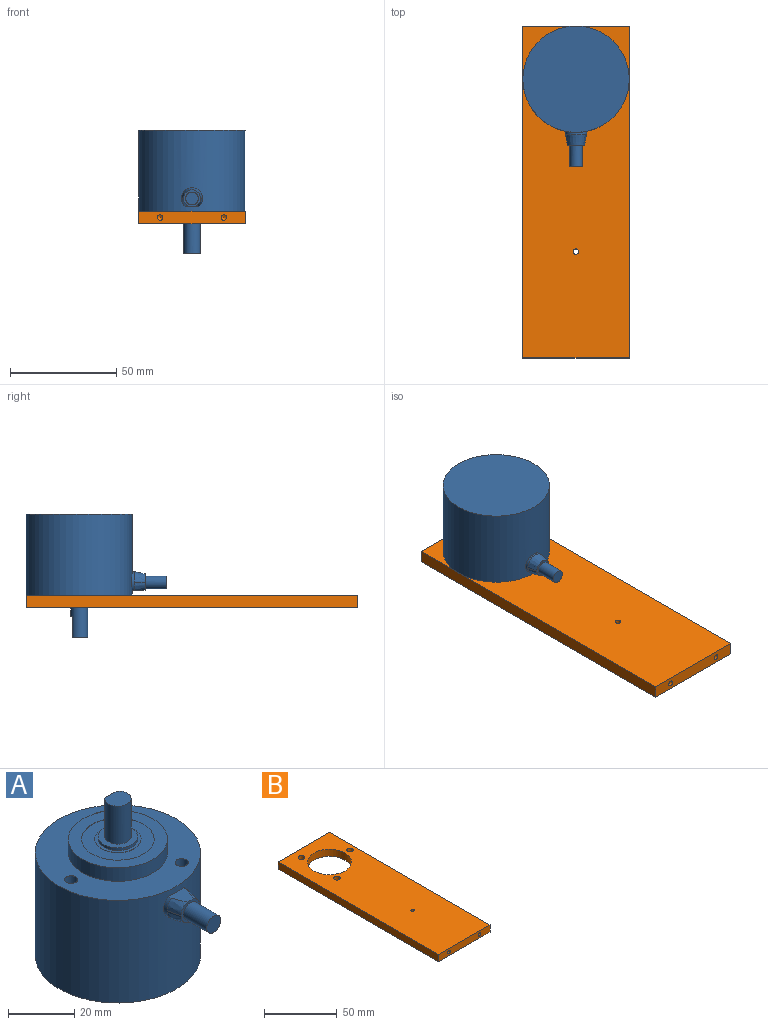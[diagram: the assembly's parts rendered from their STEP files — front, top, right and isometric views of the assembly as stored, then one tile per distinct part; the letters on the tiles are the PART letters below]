
ASSEMBLY  parts=2 mates=1
PART A: 29 faces, bbox 51.1x67.1x59.1 mm
  f0: plane 5.29x1mm, normal (0,0,1), area 3.6mm2, adj f1,f2
  f1: cylinder r=4mm len=14mm, axis (0,0,-1), area 294mm2, adj f0,f2,f3,f4
  f2: plane 10x5.29mm, normal (0,1,0), area 52.9mm2, adj f0,f1,f4
  f3: plane 12x12mm, normal (0,0,1), area 62.8mm2, adj f1,f5
  f4: plane 8x7mm, normal (0,0,1), area 46.6mm2, adj f1,f2
  f5: cylinder r=6mm len=12mm, axis (0,0,-1), area 37.7mm2, adj f3,f6
  f6: plane 14x14mm, normal (0,0,1), area 40.8mm2, adj f5,f7
  f7: cylinder r=7mm len=14mm, axis (0,0,1), area 4.4mm2, adj f6,f8
  f8: plane 22x22mm, normal (0,0,1), area 226.2mm2, adj f7,f9
  f9: cylinder r=11mm len=22mm, axis (0,0,1), area 6.9mm2, adj f8,f10
  f10: plane 30x30mm, normal (0,0,1), area 326.7mm2, adj f9,f11
  f11: cylinder r=15mm len=30mm, axis (0,0,-1), area 471.2mm2, adj f10,f12
  f12: plane 50x50mm, normal (0,0,1), area 1218.9mm2, adj f11,f13,f14,f15,f16
  f13: cylinder r=2mm len=5mm, axis (0,0,1), area 62.8mm2, adj f12,f17
  f14: cylinder r=2mm len=5mm, axis (0,0,1), area 62.8mm2, adj f12,f18
  f15: cylinder r=2mm len=5mm, axis (0,0,1), area 62.8mm2, adj f12,f19
  f16: cylinder r=25mm len=50mm, axis (0,0,1), area 5895.6mm2, adj f12,f20,f21,f22
  f17: plane 4x4mm, normal (0,0,1), area 12.6mm2, adj f13
  f18: plane 4x4mm, normal (0,0,1), area 12.6mm2, adj f14
  f19: plane 4x4mm, normal (0,0,1), area 12.6mm2, adj f15
  f20: plane 6.93x6.64mm, normal (0,0,1), area 30.6mm2, adj f16,f22,f23,f24,f25
  f21: plane 50x50mm, normal (0,0,-1), area 1963.5mm2, adj f16
  f22: cylinder r=5mm len=10mm, axis (0,-1,0), area 26.9mm2, adj f16,f20,f24,f25,f26
  f23: plane 9.13x8.93mm, normal (0,-1,0), area 21.7mm2, adj f20,f24,f25,f26,f27
  f24: bspline ~5x4.75mm, area 24mm2, adj f20,f22,f23,f26
  f25: bspline ~5x4.77mm, area 24mm2, adj f20,f22,f23,f26
  f26: bspline ~10x10mm, area 72.1mm2, adj f22,f23,f24,f25
  f27: cylinder r=3mm len=10mm, axis (0,1,0), area 188.5mm2, adj f23,f28
  f28: plane 6x6mm, normal (0,-1,0), area 28.3mm2, adj f27
PART B: 15 faces, bbox 50x156x6 mm
  f0: plane 50x6mm, normal (0,-1,0), area 290.2mm2, adj f1,f3,f4,f5,f12,f14
  f1: plane 156x6mm, normal (1,0,0), area 936mm2, adj f0,f2,f4,f5
  f2: plane 50x6mm, normal (0,1,0), area 300mm2, adj f1,f3,f4,f5
  f3: plane 156x6mm, normal (-1,0,0), area 936mm2, adj f0,f2,f4,f5
  f4: plane 156x50mm, normal (0,0,1), area 7031.1mm2, adj f0,f1,f2,f3,f6,f7,f8,f9
  f5: plane 156x50mm, normal (0,0,-1), area 7031.1mm2, adj f0,f1,f2,f3,f6,f7,f8,f9
  f6: cylinder r=2.25mm len=6mm, axis (0,0,1), area 84.8mm2, adj f4,f5
  f7: cylinder r=2.25mm len=6mm, axis (0,0,1), area 84.8mm2, adj f4,f5
  f8: cylinder r=15.1mm len=30.2mm, axis (0,0,1), area 569.3mm2, adj f4,f5
  f9: cylinder r=2.25mm len=6mm, axis (0,0,1), area 84.8mm2, adj f4,f5
  f10: cylinder r=1.25mm len=6mm, axis (0,0,1), area 47.1mm2, adj f4,f5
  f11: cone r=0mm half-angle=59deg, axis (0,-1,0), area 5.7mm2, adj f12
  f12: cylinder r=1.25mm len=15mm, axis (0,-1,0), area 117.8mm2, adj f0,f11
  f13: cone r=0mm half-angle=59deg, axis (0,-1,0), area 5.7mm2, adj f14
  f14: cylinder r=1.25mm len=15mm, axis (0,-1,0), area 117.8mm2, adj f0,f13
PLACE A rot(axis=(0,1,0),180deg) t=(52.41,71.26,-15)mm
PLACE B t=(52.41,18.26,-21)mm
MATE fastened A.f14 <-> B.f9  axis (0,0,-1) through (72.41,71.26,-15)mm
